# Revit family: cb1d7ae6-7edb-44c9-99e2-a85304ea1d1f
name_source: partatom
category: Pipe Fittings
revit_build: Autodesk Revit 2016 (Build: 20161004_0715(x64)
units: mm (PartAtom-declared; Revit-internal decimal feet)

## family parameters
Always vertical = Yes
Cut with Voids When Loaded = No
OmniClass Number = 23.60.30.11.14
OmniClass Title = Pipework Fittings
Part Type = Union
Round Connector Dimension = Use Radius
Shared = No
Work Plane-Based = No

## types (1)
- Standard
    04 CSI = 22 00 00
    95 CSI = 15100
    Assembly Code = D2090800
    CADworks URL = http://www.CADworks.net
    Compression Liner Material = Rubber - Schott
    Coupling Band Material = Steel - Schott - Stainless
    Description = Bend Offset
    K Coefficient Table = Regular 45, 90 and 180 Elbow
    Lookup Table Name = Bend_Offset-Schott-Kimax-6513
    Loss Method = K Coefficient from Table
    Manufacturer = SCHOTT
    Model = 6513-1590, 6513-1560, 6513-1545, 6513-1522, 6513-2090, 6513-2060, 6513-2045, 6513-2022, 6513-3090, 6513-3060, 6513-3045, 6513-3022, 6513-4090, 6513-4060, 6513-4045, 6513-4022, 6513-6045
    Pipe Material = Glass - Schott - Borosilicate
    Product URL = http://www.us.schott.com
    Seal Ring Material = Teflon - Schott
    Series = Kimax
    Subcategory = Bend Fitting
    URL = http://www.us.schott.com

## geometry (parser evidence)
native form markers: Blend x9, Revolve x4, Sweep x5
no freeform markers — native parametric forms only
